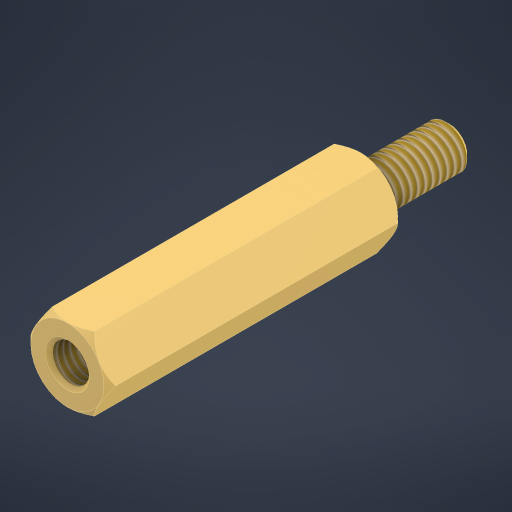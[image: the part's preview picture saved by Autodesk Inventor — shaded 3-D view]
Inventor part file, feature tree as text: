
AUTODESK INVENTOR PART (.ipt)
format: ipt  version: 2023 (Build 270158000, 158)  size: 232,960 bytes
history: mixed  units: in
note: dims shown in document units (in); Inventor stores cm internally (conversion verified against a paired STEP export)
features: thread x2, other x1, imported_body x1
ambient origin geometry x8: Origin, YZ Plane, XZ Plane, XY Plane, X Axis, Y Axis, Z Axis, Center Point
bodies: Solid1 (imported_parasolid)
feature tree (4):
  thread  "Thread1"  [1 undecoded]
  thread  "Thread2"  [1 undecoded]
  other  "InnerChamfer"
  imported_body  NMx_Import_Brep_tag  [imported B-rep: ~6 faces, bbox_mm=None]
note: 2 required parameter values undecoded (feature->parameter linkage not recoverable at this tier; creation-order binding heuristic only, values carry confidence <= 0.55)
